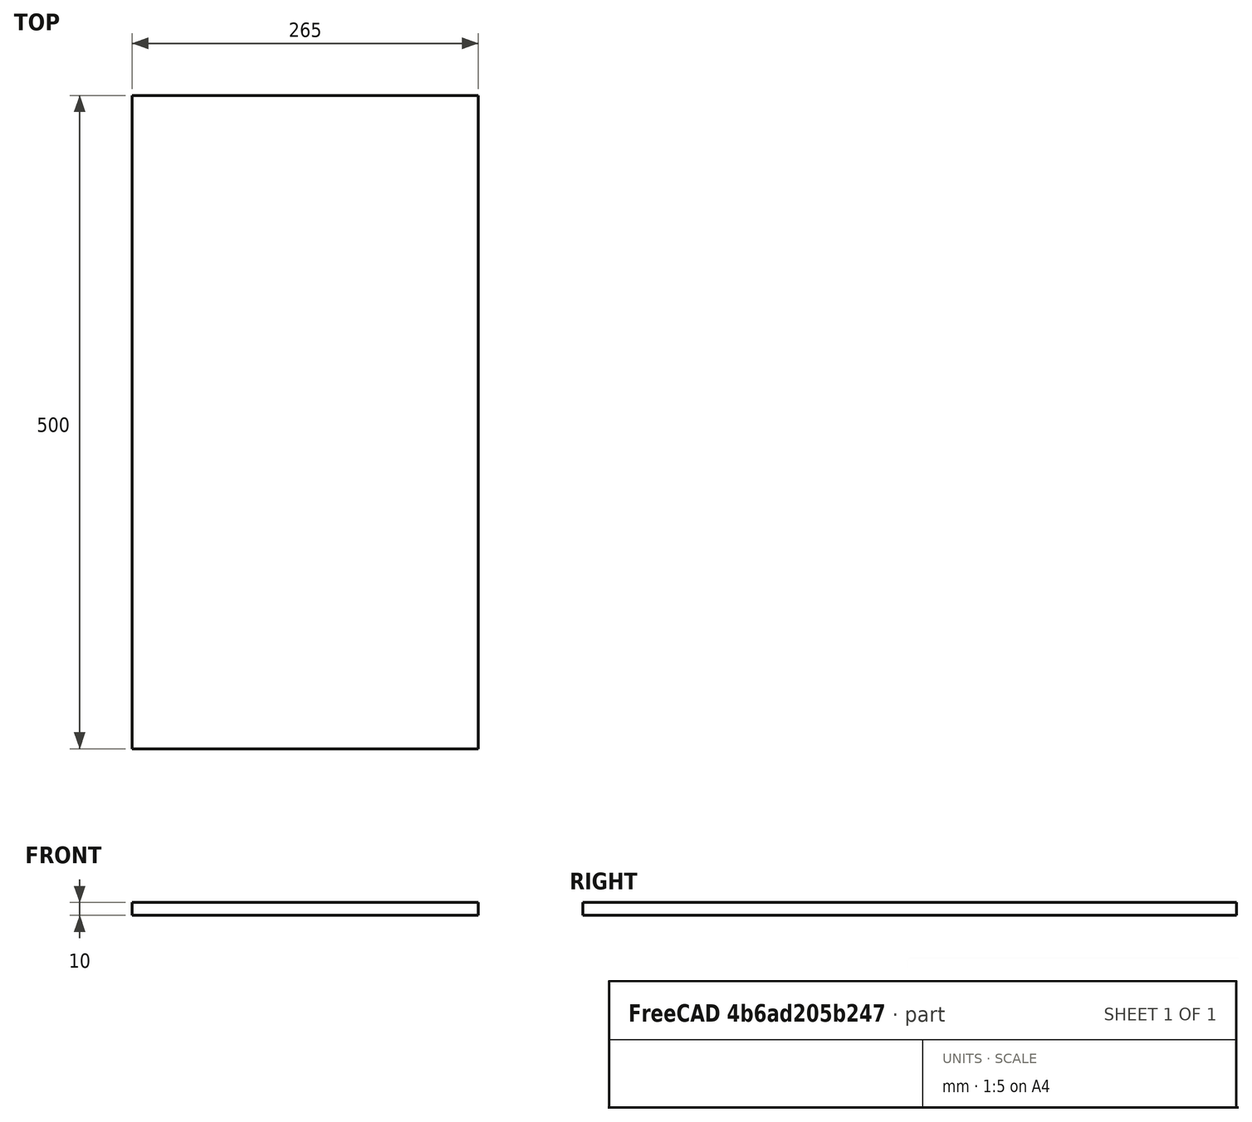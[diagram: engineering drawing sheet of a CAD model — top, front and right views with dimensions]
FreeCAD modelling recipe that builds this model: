
FCSTD DOCUMENT  (FreeCAD 0.19R24276 (Git))
Label: 7002_Marquee_top
License: All rights reserved
LicenseURL: http://en.wikipedia.org/wiki/All_rights_reserved
objects: Sketcher::SketchObject×1, PartDesign::Pad×1, PartDesign::Body×1, Spreadsheet::Sheet×1
note: 4 computed .brp shape members not serialized (recipe doc carries the construction recipe); baked Part::Feature solids carry a one-line shape summary decoded from their .brp

FEATURE [Sketcher::SketchObject] Sketch
  FullyConstrained = false
  MapMode = 5
  Support = -> [XY_Plane]
  expr: Constraints[5] = <<xls>>.k_w
  expr: Constraints[6] = <<xls>>.k_d
  sketch-geometry (5):
    g0: LineSegment StartX=0 StartY=500 StartZ=0 EndX=265 EndY=500 EndZ=0
    g1: LineSegment StartX=265 StartY=500 StartZ=0 EndX=265 EndY=0 EndZ=0
    g2: LineSegment StartX=265 StartY=0 StartZ=0 EndX=0 EndY=0 EndZ=0
    g3: LineSegment StartX=0 StartY=0 StartZ=0 EndX=0 EndY=250 EndZ=0
    g4: LineSegment StartX=0 StartY=250 StartZ=0 EndX=0 EndY=500 EndZ=0
  constraints (14):
    c: Coincident(g0,g1)
    c: Coincident(g1,g2)
    c: Horizontal(g0)
    c: Horizontal(g2)
    c: Vertical(g1)
    c: DistanceY(g1,g1) = 500
    c: DistanceX(g0,g0) = 265
    c: Coincident(g3,g2)
    c: Coincident(g4,g0)
    c: Equal(g3,g4)
    c: Vertical(g4)
    c: Vertical(g3)
    c: Coincident(g3,g4)
    c: Coincident(g2,g-1)
FEATURE [PartDesign::Pad] Pad
  AllowMultiFace = false
  Direction = (1,1,1)
  Length = 10
  Length2 = 100
  Profile = -> Sketch
  Type = 0
  expr: Length = <<xls>>.k_t_0
FEATURE [PartDesign::Body] Body
  Group = -> [Sketch,Pad]
  Origin = -> Origin
  Tip = -> Pad
FEATURE [Spreadsheet::Sheet] Spreadsheet  label="xls"
  cells = B3=Marquee Top; B4=Orientation; D4=(0,0,1); B5=Thickness; C5=k_t_0; D5(k_t_0)=10; E5=mm; F5=10,13,16,19; B6=Width Y; C6=k_w; D6(k_w)=500; E6=mm; B7=Deapth X; C7=k_d; D7(k_d)=265; E7=mm
